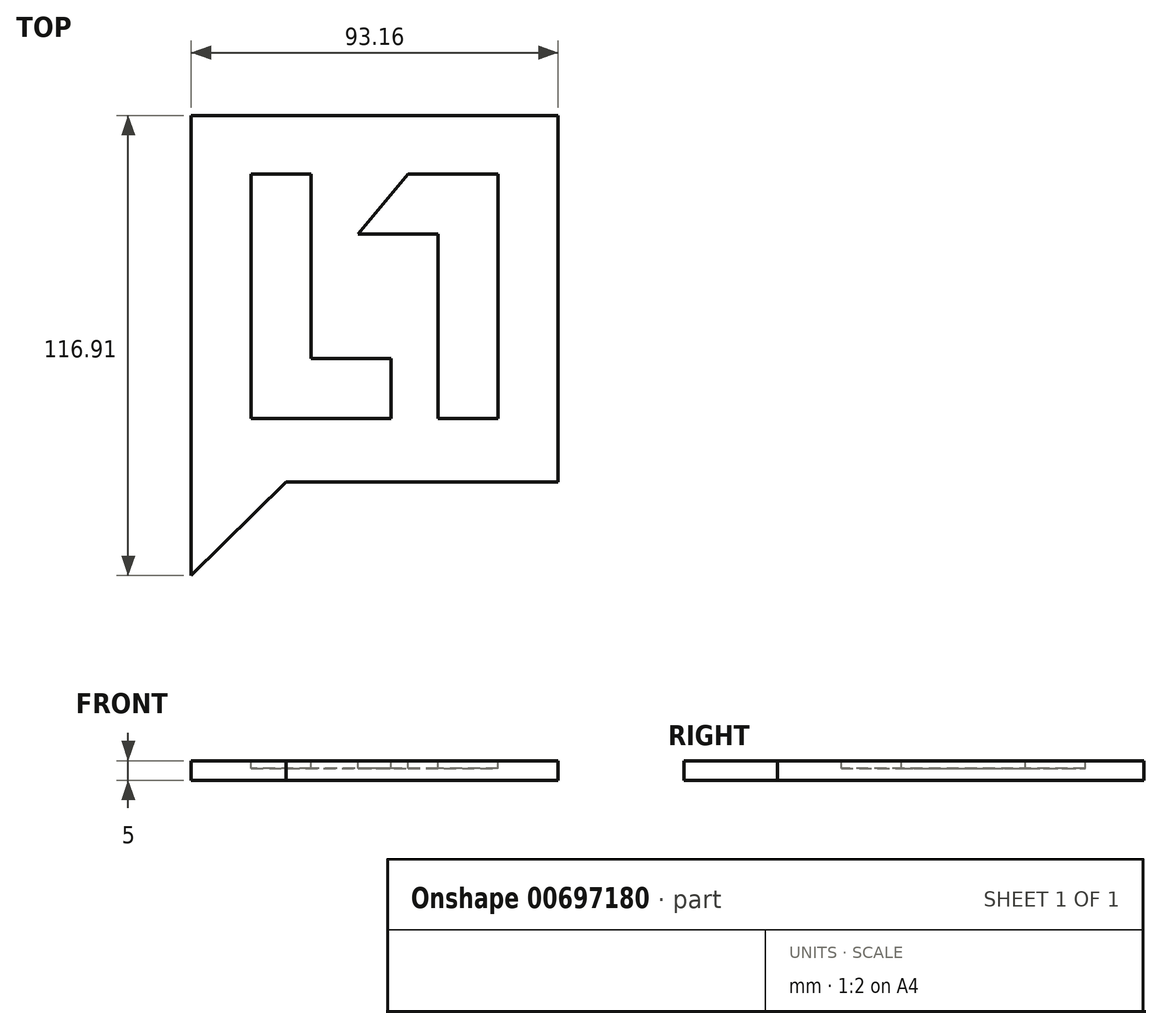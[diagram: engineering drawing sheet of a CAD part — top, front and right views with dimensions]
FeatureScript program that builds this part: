
annotation { "Feature Type Name" : "Feature", "Feature Type Description" : "" }
export const myFeature = defineFeature(function(context is Context, id is Id, definition is map)
    precondition{}
    {
        {
            var Q0;
            Q0=qCreatedBy(makeId("Top.planeOp"),FACE);
            var sketch = newSketch(context, id + "F0", { "sketchPlane" : qUnion([Q0])});
            skLineSegment(sketch, "E0", {"start": v(-55.59, 49.25) * mm, "end": v(-55.59, -67.66) * mm});
            skLineSegment(sketch, "E1", {"start": v(-55.59, -67.66) * mm, "end": v(-31.56, -43.86) * mm});
            skLineSegment(sketch, "E2", {"start": v(-31.56, -43.86) * mm, "end": v(37.57, -43.86) * mm});
            skLineSegment(sketch, "E3", {"start": v(37.57, -43.86) * mm, "end": v(37.57, 49.25) * mm});
            skLineSegment(sketch, "E4", {"start": v(-55.59, 49.25) * mm, "end": v(37.57, 49.25) * mm});
            skSolve(sketch);
        }
        {
            var Q0;
            Q0 = qSketchRegion(id + "F0", true);
            extrude(context, id + "F1", {"entities" : qUnion([Q0]), "depth" : 5 * mm, "offsetDistance" : 25.4 * mm});
        }
        {
            var Q0;
            Q0=makeQuery(id+"F1.opExtrude","CAP_FACE",FACE,{"disambiguationData":[OSD([sQuery(id+"F0.wireOp",EDGE,"E0"),sQuery(id+"F0.wireOp",EDGE,"E1"),sQuery(id+"F0.wireOp",EDGE,"E2"),sQuery(id+"F0.wireOp",EDGE,"E3"),sQuery(id+"F0.wireOp",EDGE,"E4")])],"isStart":false});
            var sketch = newSketch(context, id + "F2", { "sketchPlane" : qUnion([Q0])});
            skLineSegment(sketch, "E5", {"start": v(-40.35, 34.34) * mm, "end": v(-40.35, -27.7) * mm});
            skLineSegment(sketch, "E6", {"start": v(-40.35, -27.7) * mm, "end": v(-4.79, -27.7) * mm});
            skLineSegment(sketch, "E7", {"start": v(-4.79, -27.7) * mm, "end": v(-4.79, -12.45) * mm});
            skLineSegment(sketch, "E8", {"start": v(-4.79, -12.45) * mm, "end": v(-25.1, -12.45) * mm});
            skLineSegment(sketch, "E9", {"start": v(-25.1, -12.45) * mm, "end": v(-25.1, 34.34) * mm});
            skLineSegment(sketch, "E10", {"start": v(-25.1, 34.34) * mm, "end": v(-40.35, 34.34) * mm});
            skLineSegment(sketch, "E11", {"start": v(-0.53, 34.34) * mm, "end": v(22.33, 34.34) * mm});
            skLineSegment(sketch, "E12", {"start": v(22.33, 34.34) * mm, "end": v(22.33, -27.7) * mm});
            skLineSegment(sketch, "E13", {"start": v(22.33, -27.7) * mm, "end": v(7.1, -27.7) * mm});
            skLineSegment(sketch, "E14", {"start": v(7.1, -27.7) * mm, "end": v(7.1, 19.1) * mm});
            skLineSegment(sketch, "E15", {"start": v(7.1, 19.1) * mm, "end": v(-13.23, 19.1) * mm});
            skLineSegment(sketch, "E16.0", {"start": v(-13.23, 19.1) * mm, "end": v(-0.53, 34.34) * mm});
            skPoint(sketch, "E17.orphan", {"position": v(-3.04, 34.34) * mm});
            skPoint(sketch, "E18.orphan", {"position": v(-19.1, 19.1) * mm});
            skSolve(sketch);
        }
        {
            var Q0;
            Q0 = qSketchRegion(id + "F2", true);
            extrude(context, id + "F3", {"entities" : qUnion([Q0]), "operationType" : NewBodyOperationType.REMOVE, "oppositeDirection" : true, "depth" : 2 * mm, "offsetDistance" : 25.4 * mm});
        }
    });
